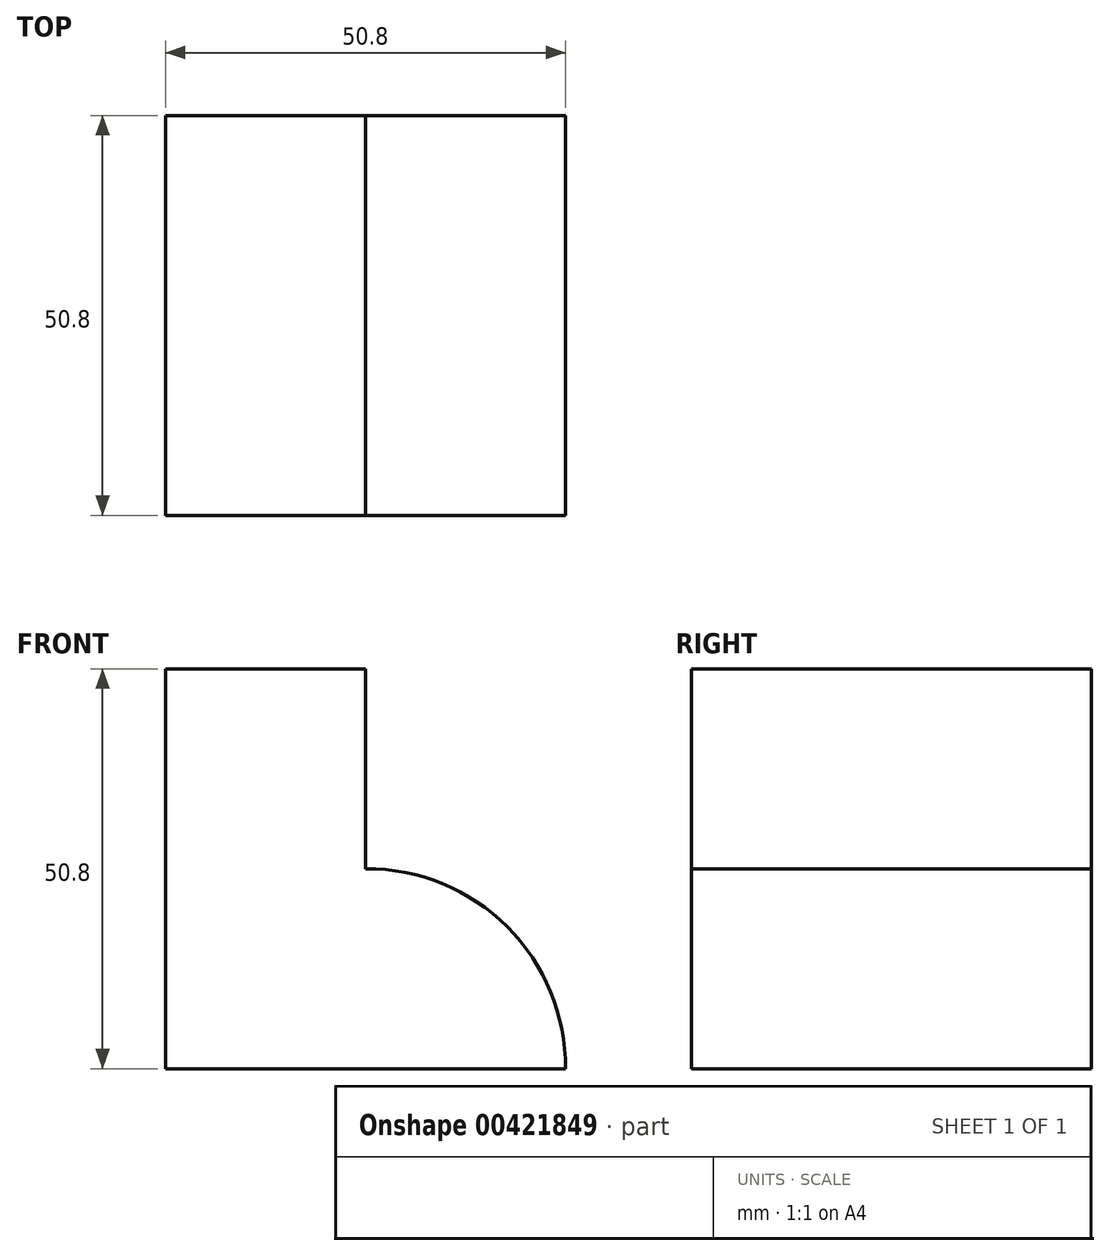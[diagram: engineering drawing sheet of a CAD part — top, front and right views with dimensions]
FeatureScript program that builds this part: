
annotation { "Feature Type Name" : "Feature", "Feature Type Description" : "" }
export const myFeature = defineFeature(function(context is Context, id is Id, definition is map)
    precondition{}
    {
        {
            var Q0;
            Q0=qCreatedBy(makeId("Front.planeOp"),FACE);
            var sketch = newSketch(context, id + "F0", { "sketchPlane" : qUnion([Q0])});
            skLineSegment(sketch, "E0", {"start": v(0, 0) * mm, "end": v(-50.8, 0) * mm});
            skLineSegment(sketch, "E1", {"start": v(-50.8, 0) * mm, "end": v(-50.8, 50.8) * mm});
            skLineSegment(sketch, "E2", {"start": v(-50.8, 50.8) * mm, "end": v(-25.4, 50.8) * mm});
            skLineSegment(sketch, "E3", {"start": v(-25.4, 50.8) * mm, "end": v(-25.4, 25.4) * mm});
            skArc(sketch, "E4", {"start": v(0, 0) * mm, "mid": v(-7.4, 18) * mm, "end": v(-25.4, 25.4) * mm});
            skSolve(sketch);
        }
        {
            var Q0;
            Q0 = qSketchRegion(id + "F0", true);
            extrude(context, id + "F1", {"entities" : qUnion([Q0]), "depth" : 50.8 * mm});
        }
    });
